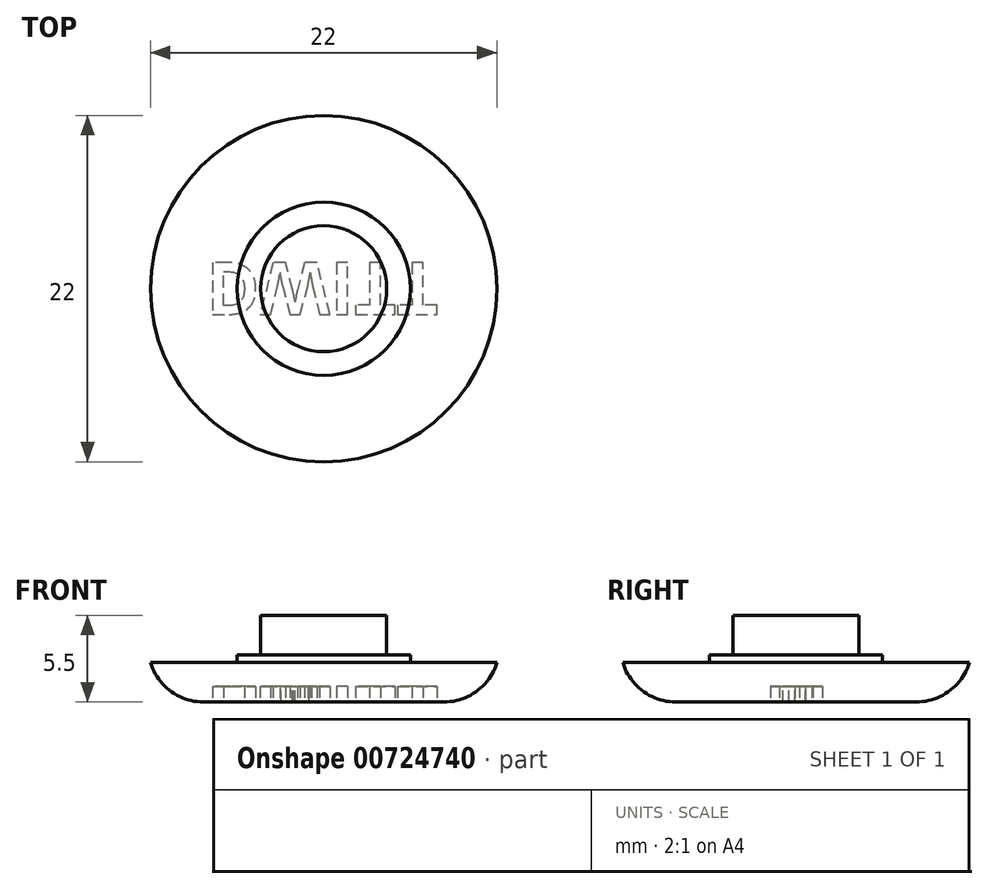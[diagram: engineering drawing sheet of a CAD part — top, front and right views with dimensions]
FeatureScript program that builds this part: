
annotation { "Feature Type Name" : "Feature", "Feature Type Description" : "" }
export const myFeature = defineFeature(function(context is Context, id is Id, definition is map)
    precondition{}
    {
        {
            var Q0;
            Q0=qCreatedBy(makeId("Top.planeOp"),FACE);
            var sketch = newSketch(context, id + "F0", { "sketchPlane" : qUnion([Q0])});
            skCircle(sketch, "E0", {"center": v(0, 0) * mm, "radius": 11 * mm});
            skCircle(sketch, "E1", {"center": v(0, 0) * mm, "radius": 4 * mm});
            skCircle(sketch, "E2", {"center": v(0, 0) * mm, "radius": 5.5 * mm});
            skSolve(sketch);
        }
        {
            var Q0;
            Q0=makeQuery(id+"F0.imprint","IMPRINT",FACE,{"disambiguationData":[TD([[makeQuery(id+"F0.imprint","IMPRINT",EDGE,{"derivedFrom":sQuery(id+"F0.wireOp",EDGE,"E0")}),1.0]])]});
            extrude(context, id + "F1", {"entities" : qUnion([Q0]), "depth" : 2.5 * mm, "offsetDistance" : 25 * mm});
        }
        {
            var Q0;
            Q0=makeQuery(id+"F0.imprint","IMPRINT",FACE,{"disambiguationData":[TD([[makeQuery(id+"F0.imprint","IMPRINT",EDGE,{"derivedFrom":sQuery(id+"F0.wireOp",EDGE,"E1")}),-1.0]])]});
            var Q1;
            Q1=makeQuery(id+"F1.opExtrude","CAP_FACE",FACE,{"disambiguationData":[OSD([sQuery(id+"F0.wireOp",EDGE,"E0"),sQuery(id+"F0.wireOp",EDGE,"E2")])],"isStart":false});
            extrude(context, id + "F2", {"entities" : qUnion([Q0]), "operationType" : NewBodyOperationType.ADD, "endBound" : BoundingType.UP_TO_SURFACE, "depth" : 25 * mm, "endBoundEntityFace" : qUnion([Q1]), "hasOffset" : true, "offsetDistance" : .5 * mm, "offsetOppositeDirection" : true});
        }
        {
            var Q0;
            Q0=makeQuery(id+"F0.imprint","IMPRINT",FACE,{"disambiguationData":[TD([[makeQuery(id+"F0.imprint","IMPRINT",EDGE,{"derivedFrom":sQuery(id+"F0.wireOp",EDGE,"E1")}),1.0]])]});
            var Q1;
            Q1=makeQuery(id+"F2.opExtrude","CAP_FACE",FACE,{"disambiguationData":[OSD([sQuery(id+"F0.wireOp",EDGE,"E0"),sQuery(id+"F0.wireOp",EDGE,"E2")])],"isStart":false});
            extrude(context, id + "F3", {"entities" : qUnion([Q0]), "operationType" : NewBodyOperationType.ADD, "endBound" : BoundingType.UP_TO_SURFACE, "depth" : 3 * mm, "endBoundEntityFace" : qUnion([Q1]), "hasOffset" : true, "offsetDistance" : 2.5 * mm, "offsetOppositeDirection" : true});
        }
        {
            var Q0;
            {var subQ0=sQuery(id+"F0.wireOp",EDGE,"E1");var subQ1=sQuery(id+"F0.wireOp",EDGE,"E2");Q0=makeQuery(id+"F3.boolean.opBoolean","MERGE",FACE,{"derivedFrom":[makeQuery(id+"F2.boolean.opBoolean","MERGE",FACE,{"derivedFrom":[makeQuery(id+"F1.opExtrude","CAP_FACE",FACE,{"disambiguationData":[OSD([sQuery(id+"F0.wireOp",EDGE,"E0"),subQ1])],"isStart":true}),makeQuery(id+"F2.opExtrude","CAP_FACE",FACE,{"disambiguationData":[OSD([subQ0,subQ1])],"isStart":true})]}),makeQuery(id+"F3.opExtrude","CAP_FACE",FACE,{"disambiguationData":[OSD([subQ0])],"isStart":true})]});}
            fillet(context, id + "F4", {"entities" : qUnion([Q0]), "radius" : 3.5 * mm, "tangentPropagation" : true, "allowEdgeOverflow" : false});
        }
        {
            var Q0;
            Q0=qCreatedBy(makeId("Right.planeOp"),FACE);
            var sketch = newSketch(context, id + "F5", { "sketchPlane" : qUnion([Q0])});
            skEllipse(sketch, "E3", {"center": v(-63.43, -1.89) * mm, "majorRadius": 11 * mm, "minorRadius": 2.5 * mm, "majorAxis": v(-1, 0)});
            skPoint(sketch, "E4", {"position": v(-63.43, 0.61) * mm});
            skLineSegment(sketch, "E5", {"start": v(-55.79, 0) * mm, "end": v(-71.08, 0) * mm});
            skArc(sketch, "E6", {"start": v(4.15, 3.3) * mm, "mid": v(11.14, 3.63) * mm, "end": v(4.15, 3.44) * mm});
            skArc(sketch, "E7", {"start": v(-11.15, 3.45) * mm, "mid": v(-11.14, 3.38) * mm, "end": v(-11.14, 3.3) * mm});
            skLineSegment(sketch, "E8", {"start": v(-63.43, 0.61) * mm, "end": v(-63.43, -4.39) * mm});
            skPoint(sketch, "E9.orphan", {"position": v(-63.43, -3.78) * mm});
            skPoint(sketch, "E10.orphan", {"position": v(-63.43, 0) * mm});
            skSolve(sketch);
        }
        {
            var Q0;
            {var subQ0=sQuery(id+"F0.wireOp",EDGE,"E1");var subQ1=sQuery(id+"F0.wireOp",EDGE,"E2");Q0=makeQuery(id+"F3.boolean.opBoolean","MERGE",FACE,{"derivedFrom":[makeQuery(id+"F2.boolean.opBoolean","MERGE",FACE,{"derivedFrom":[makeQuery(id+"F1.opExtrude","CAP_FACE",FACE,{"disambiguationData":[OSD([sQuery(id+"F0.wireOp",EDGE,"E0"),subQ1])],"isStart":true}),makeQuery(id+"F2.opExtrude","CAP_FACE",FACE,{"disambiguationData":[OSD([subQ0,subQ1])],"isStart":true})]}),makeQuery(id+"F3.opExtrude","CAP_FACE",FACE,{"disambiguationData":[OSD([subQ0])],"isStart":true})]});}
            var sketch = newSketch(context, id + "F6", { "sketchPlane" : qUnion([Q0])});
            skText(sketch, "E11", { "text": "DWITT", "fontName": "OpenSans-Bold.ttf"});
            const initialGuessF6  = {"E11": [-0.00746, -0.00166, 1, 0, 0.00332]};
            skSetInitialGuess(sketch, initialGuessF6);
            skSolve(sketch);
        }
        {
            var Q0;
            Q0=qSketchRegion(id+"F6",true);
            extrude(context, id + "F7", {"entities" : qUnion([Q0]), "operationType" : NewBodyOperationType.REMOVE, "oppositeDirection" : true, "depth" : 1 * mm, "offsetDistance" : 25 * mm});
        }
    });
